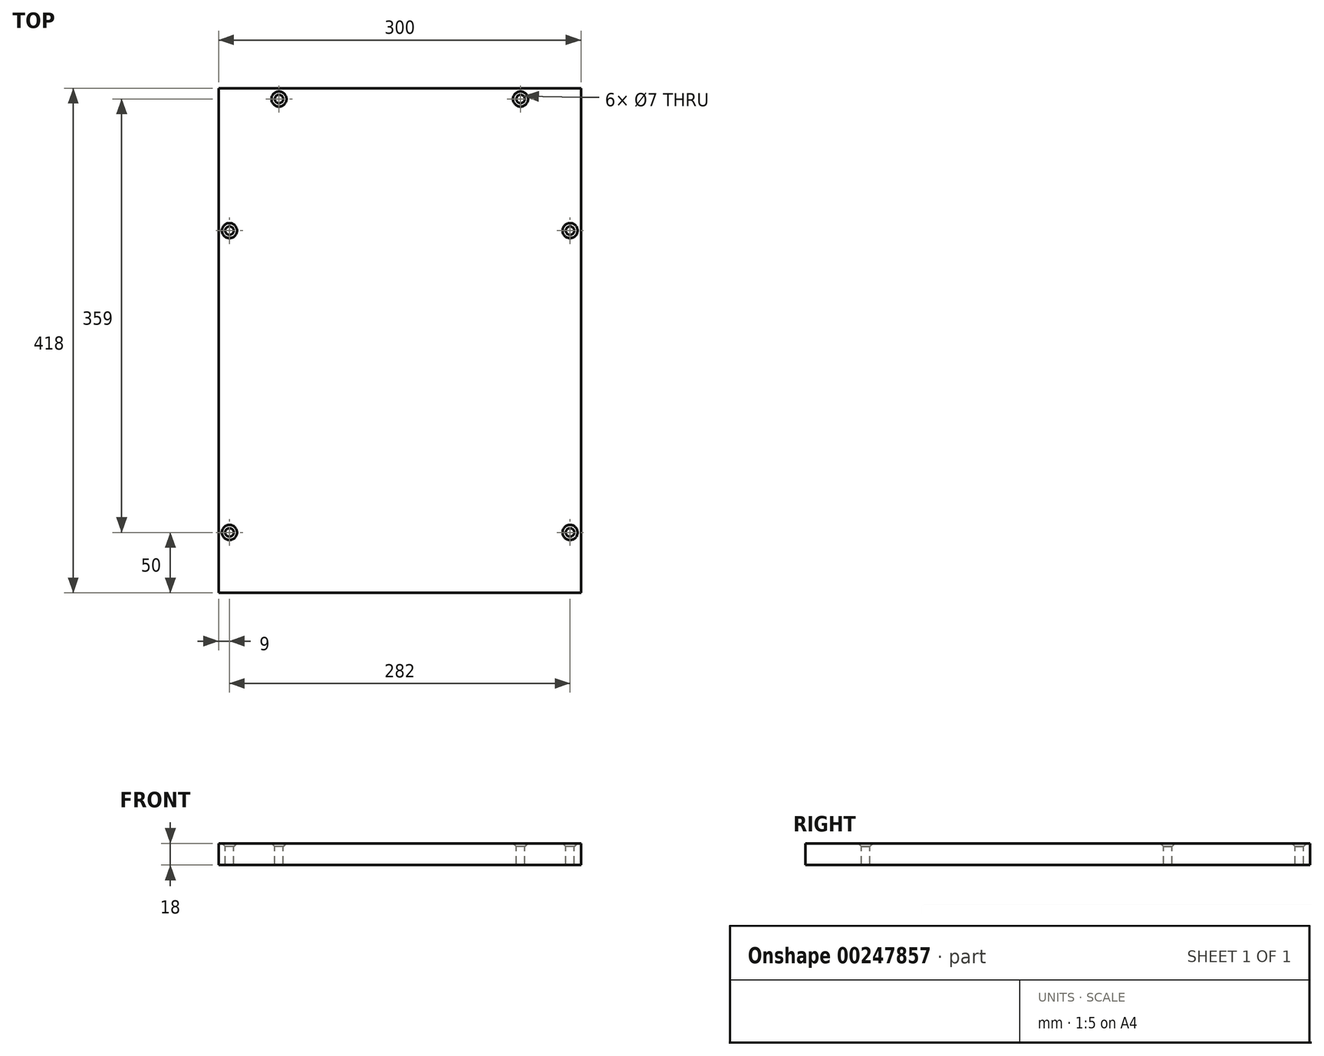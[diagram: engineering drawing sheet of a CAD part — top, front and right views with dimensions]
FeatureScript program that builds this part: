
annotation { "Feature Type Name" : "Feature", "Feature Type Description" : "" }
export const myFeature = defineFeature(function(context is Context, id is Id, definition is map)
    precondition{}
    {
        {
            var Q0;
            Q0=qCreatedBy(makeId("Top.planeOp"),FACE);
            var sketch = newSketch(context, id + "F3", { "sketchPlane" : qUnion([Q0])});
            skLineSegment(sketch, "E0.bottom", {"start": v(0, 0) * mm, "end": v(300, 0) * mm});
            skLineSegment(sketch, "E0.top", {"start": v(0, 418) * mm, "end": v(300, 418) * mm});
            skLineSegment(sketch, "E0.left", {"start": v(0, 0) * mm, "end": v(0, 418) * mm});
            skLineSegment(sketch, "E0.right", {"start": v(300, 0) * mm, "end": v(300, 418) * mm});
            skSolve(sketch);
        }
        {
            var Q0;
            Q0=makeQuery(id+"F3.imprint","IMPRINT",FACE,{"disambiguationData":[TD([[makeQuery(id+"F3.imprint","IMPRINT",EDGE,{"derivedFrom":sQuery(id+"F3.wireOp",EDGE,"E0.bottom")}),1.0]])]});
            extrude(context, id + "F0", {"entities" : qUnion([Q0]), "depth" : 18 * mm});
        }
        {
            var Q0;
            Q0=makeQuery(id+"F0.opExtrude","CAP_FACE",FACE,{"disambiguationData":[OSD([sQuery(id+"F3.wireOp",EDGE,"E0.bottom"),sQuery(id+"F3.wireOp",EDGE,"E0.top"),sQuery(id+"F3.wireOp",EDGE,"E0.left"),sQuery(id+"F3.wireOp",EDGE,"E0.right")])],"isStart":false});
            var sketch = newSketch(context, id + "F1", { "sketchPlane" : qUnion([Q0])});
            skPoint(sketch, "E1", {"position": v(250, 409) * mm});
            skPoint(sketch, "E2", {"position": v(50, 409) * mm});
            skLineSegment(sketch, "E3", {"start": v(50, 409) * mm, "end": v(250, 409) * mm, "construction": true});
            skSolve(sketch);
        }
        {
            var Q0;
            Q0=makeQuery(id+"F0.opExtrude","CAP_FACE",FACE,{"disambiguationData":[OSD([sQuery(id+"F3.wireOp",EDGE,"E0.bottom"),sQuery(id+"F3.wireOp",EDGE,"E0.top"),sQuery(id+"F3.wireOp",EDGE,"E0.left"),sQuery(id+"F3.wireOp",EDGE,"E0.right")])],"isStart":false});
            var sketch = newSketch(context, id + "F4", { "sketchPlane" : qUnion([Q0])});
            skLineSegment(sketch, "E4", {"start": v(9, 300) * mm, "end": v(9, 50) * mm, "construction": true});
            skLineSegment(sketch, "E5", {"start": v(291, 300) * mm, "end": v(291, 50) * mm, "construction": true});
            skLineSegment(sketch, "E6", {"start": v(9, 50) * mm, "end": v(291, 50) * mm, "construction": true});
            skLineSegment(sketch, "E7", {"start": v(9, 300) * mm, "end": v(291, 300) * mm, "construction": true});
            skPoint(sketch, "E8", {"position": v(9, 300) * mm});
            skPoint(sketch, "E9", {"position": v(9, 50) * mm});
            skPoint(sketch, "E10", {"position": v(291, 300) * mm});
            skPoint(sketch, "E11", {"position": v(291, 50) * mm});
            skSolve(sketch);
        }
        {
            var Q0;
            Q0=sQuery(id+"F4.wireOp",VERTEX,"E6.start");
            var Q1;
            Q1=sQuery(id+"F4.wireOp",VERTEX,"E11");
            var Q2;
            Q2=sQuery(id+"F4.wireOp",VERTEX,"E8");
            var Q3;
            Q3=sQuery(id+"F4.wireOp",VERTEX,"E10");
            var Q4;
            Q4=sQuery(id+"F1.wireOp",VERTEX,"E2");
            var Q5;
            Q5=sQuery(id+"F1.wireOp",VERTEX,"E1");
            var Q6;
            Q6=makeQuery(id+"F0.opExtrude","SWEPT_BODY",BODY,{"disambiguationData":[OSD([sQuery(id+"F3.wireOp",EDGE,"E0.bottom"),sQuery(id+"F3.wireOp",EDGE,"E0.top"),sQuery(id+"F3.wireOp",EDGE,"E0.left"),sQuery(id+"F3.wireOp",EDGE,"E0.right")])]});
            hole(context, id + "F2", {"style" : HoleStyle.C_SINK, "endStyle" : HoleEndStyle.THROUGH, "holeDiameter" : 7 * mm, "cSinkDiameter" : 12.5 * mm, "cSinkAngle" : 90 * degree, "tappedDepth" : 12 * mm, "tapClearance" : 3, "locations" : qUnion([Q0, Q1, Q2, Q3, Q4, Q5]), "scope" : qUnion([Q6])});
        }
    });
